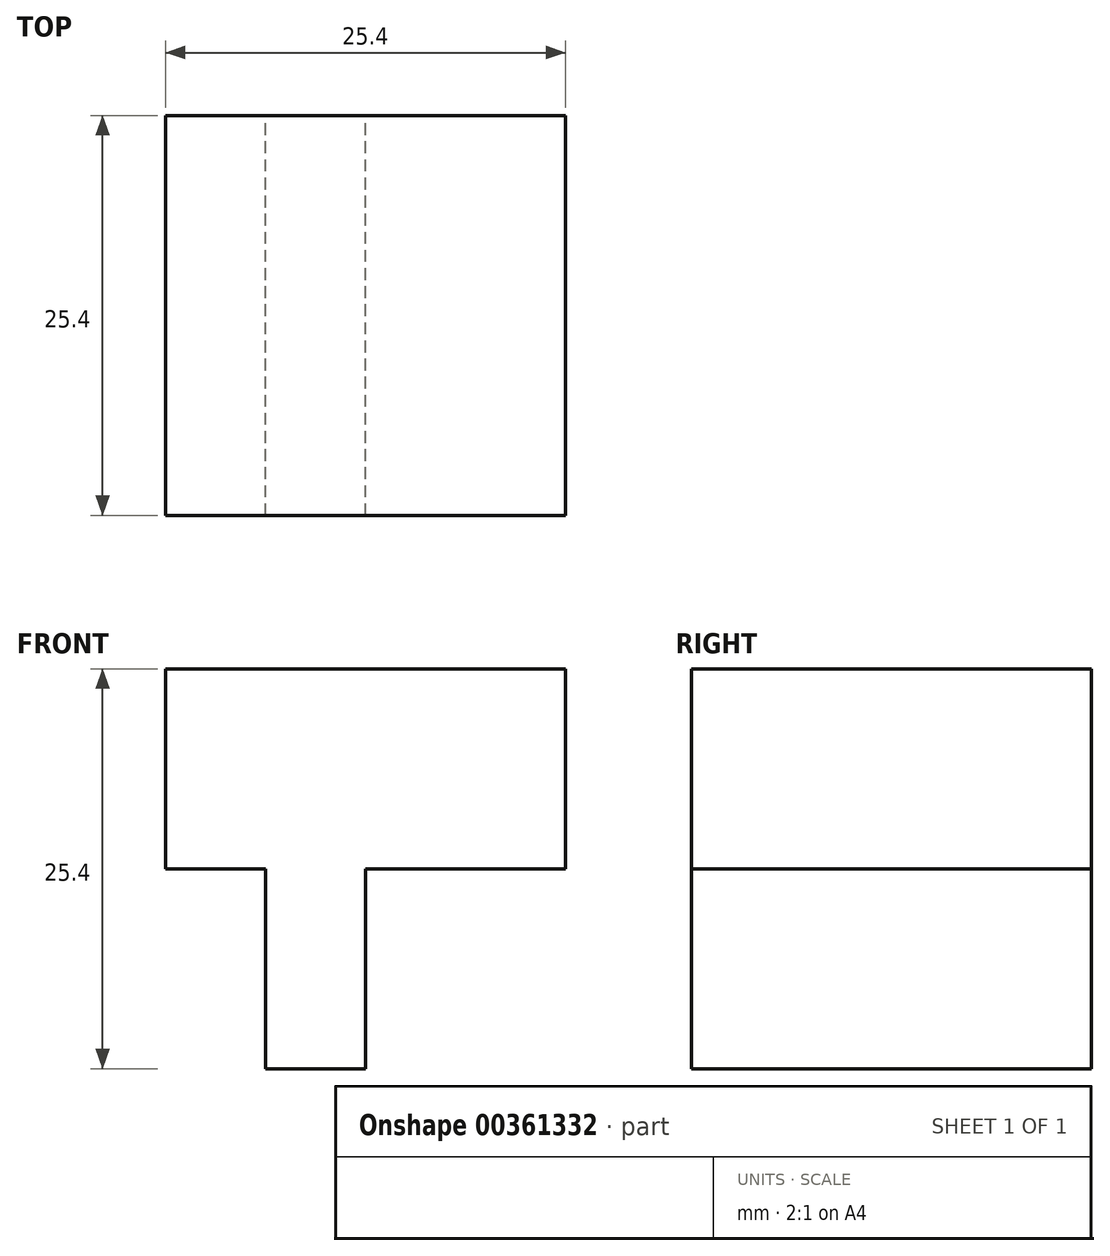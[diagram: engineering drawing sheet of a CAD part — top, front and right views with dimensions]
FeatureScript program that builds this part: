
annotation { "Feature Type Name" : "Feature", "Feature Type Description" : "" }
export const myFeature = defineFeature(function(context is Context, id is Id, definition is map)
    precondition{}
    {
        {
            var Q0;
            Q0=qCreatedBy(makeId("Front.planeOp"),FACE);
            var sketch = newSketch(context, id + "F0", { "sketchPlane" : qUnion([Q0])});
            skLineSegment(sketch, "E0", {"start": v(25.4, 0) * mm, "end": v(0, 0) * mm});
            skLineSegment(sketch, "E1", {"start": v(25.4, 0) * mm, "end": v(25.4, -12.7) * mm});
            skLineSegment(sketch, "E2", {"start": v(25.4, -12.7) * mm, "end": v(12.7, -12.7) * mm});
            skLineSegment(sketch, "E3", {"start": v(12.7, -12.7) * mm, "end": v(12.7, -25.4) * mm});
            skLineSegment(sketch, "E4", {"start": v(12.7, -25.4) * mm, "end": v(6.35, -25.4) * mm});
            skLineSegment(sketch, "E5", {"start": v(6.35, -25.4) * mm, "end": v(6.35, -12.7) * mm});
            skLineSegment(sketch, "E6", {"start": v(6.35, -12.7) * mm, "end": v(0, -12.7) * mm});
            skLineSegment(sketch, "E7", {"start": v(0, -12.7) * mm, "end": v(0, 0) * mm});
            skSolve(sketch);
        }
        {
            var Q0;
            Q0=makeQuery(id+"F0.imprint","IMPRINT",FACE,{"disambiguationData":[TD([[makeQuery(id+"F0.imprint","IMPRINT",EDGE,{"derivedFrom":sQuery(id+"F0.wireOp",EDGE,"E0")}),1.0]])]});
            extrude(context, id + "F1", {"entities" : qUnion([Q0]), "depth" : 25.4 * mm});
        }
    });
